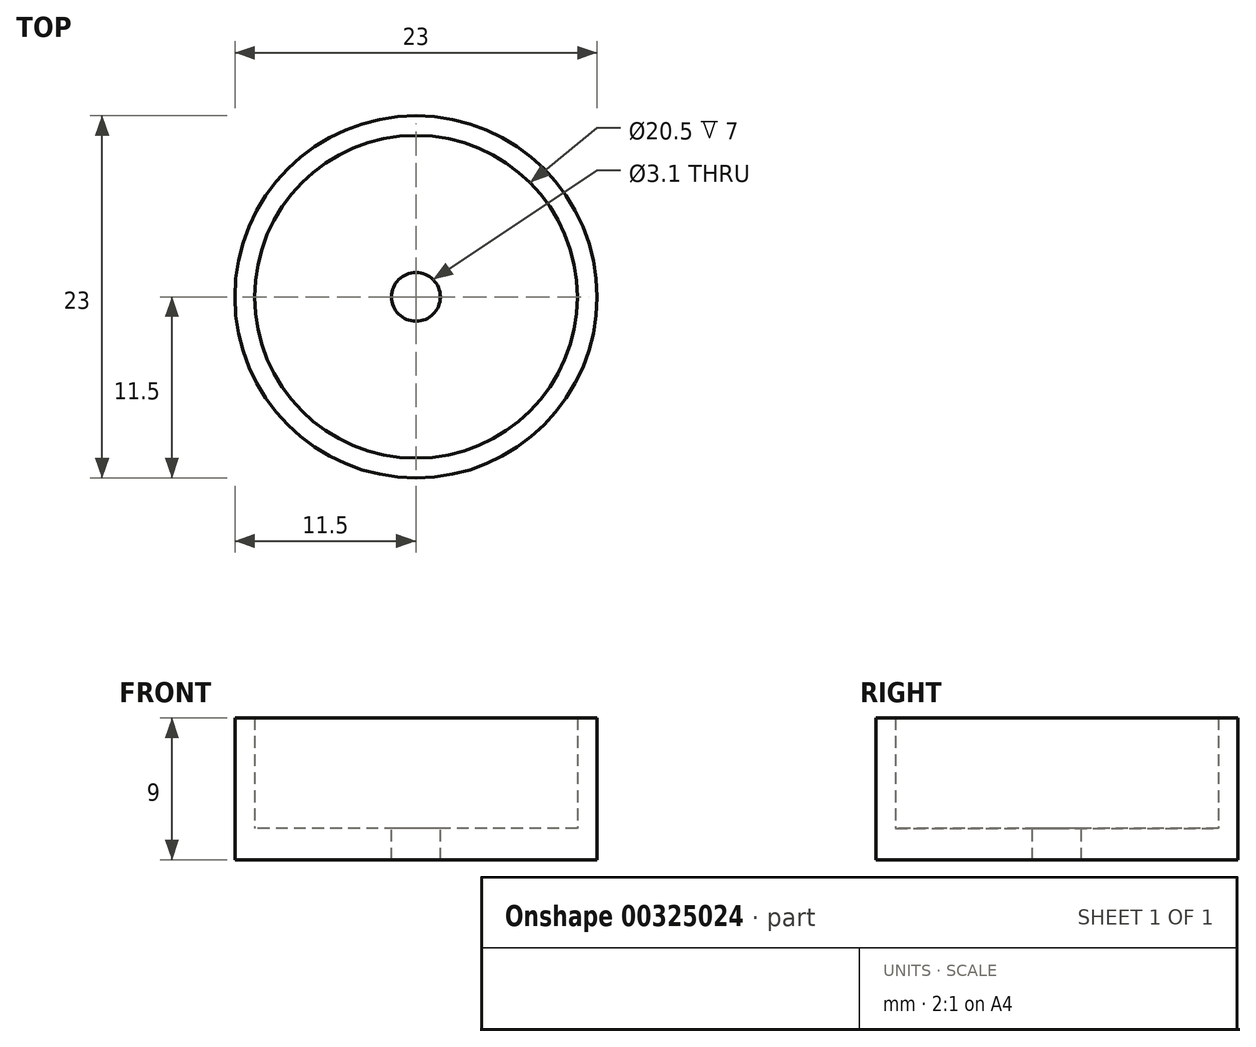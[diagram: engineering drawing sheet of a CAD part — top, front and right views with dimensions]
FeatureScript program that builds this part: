
annotation { "Feature Type Name" : "Feature", "Feature Type Description" : "" }
export const myFeature = defineFeature(function(context is Context, id is Id, definition is map)
    precondition{}
    {
        {
            var Q0;
            Q0=qCreatedBy(makeId("Top.planeOp"),FACE);
            var sketch = newSketch(context, id + "F0", { "sketchPlane" : qUnion([Q0])});
            skCircle(sketch, "E0", {"center": v(0, 0) * mm, "radius": 11.5 * mm});
            skSolve(sketch);
        }
        {
            var Q0;
            Q0=makeQuery(id+"F0.imprint","IMPRINT",FACE,{"disambiguationData":[TD([[makeQuery(id+"F0.imprint","IMPRINT",EDGE,{"derivedFrom":sQuery(id+"F0.wireOp",EDGE,"E0")}),1.0]])]});
            extrude(context, id + "F1", {"entities" : qUnion([Q0]), "depth" : 2 * mm});
        }
        {
            var Q0;
            Q0=makeQuery(id+"F1.opExtrude","CAP_FACE",FACE,{"disambiguationData":[OSD([sQuery(id+"F0.wireOp",EDGE,"E0")])],"isStart":false});
            var sketch = newSketch(context, id + "F2", { "sketchPlane" : qUnion([Q0])});
            skCircle(sketch, "E1", {"center": v(0, 0) * mm, "radius": 11.5 * mm});
            skCircle(sketch, "E2", {"center": v(0, 0) * mm, "radius": 10.25 * mm});
            skCircle(sketch, "E3", {"center": v(0, 0) * mm, "radius": 1.55 * mm});
            skSolve(sketch);
        }
        {
            var Q0;
            Q0=makeQuery(id+"F2.imprint","IMPRINT",FACE,{"disambiguationData":[TD([[makeQuery(id+"F2.imprint","IMPRINT",EDGE,{"derivedFrom":sQuery(id+"F2.wireOp",EDGE,"E1")}),1.0]])]});
            extrude(context, id + "F3", {"entities" : qUnion([Q0]), "operationType" : NewBodyOperationType.ADD, "depth" : 7 * mm});
        }
        {
            var Q0;
            Q0=makeQuery(id+"F2.imprint","IMPRINT",FACE,{"disambiguationData":[TD([[makeQuery(id+"F2.imprint","IMPRINT",EDGE,{"derivedFrom":sQuery(id+"F2.wireOp",EDGE,"E3")}),1.0]])]});
            extrude(context, id + "F4", {"entities" : qUnion([Q0]), "operationType" : NewBodyOperationType.REMOVE, "oppositeDirection" : true, "depth" : 25 * mm});
        }
    });
